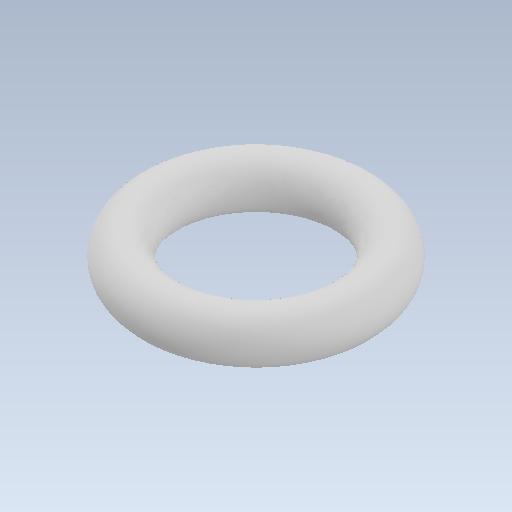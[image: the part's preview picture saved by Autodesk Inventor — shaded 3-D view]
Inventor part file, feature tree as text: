
AUTODESK INVENTOR PART (.ipt)
format: ipt  version: 2021 (Build 250183000, 183)  size: 144,384 bytes
history: native  units: mm
features: revolve x1, sketch x1
ambient origin geometry x8: Origin, YZ Plane, XZ Plane, XY Plane, X Axis, Y Axis, Z Axis, Center Point
bodies: Solid1 (feature_tree)
feature tree (2):
  revolve  "Revolution1"  [1 undecoded]
  sketch  "Sketch2"  dims[d0=90.0deg]
note: 1 required parameter value undecoded (feature->parameter linkage not recoverable at this tier; creation-order binding heuristic only, values carry confidence <= 0.55)
